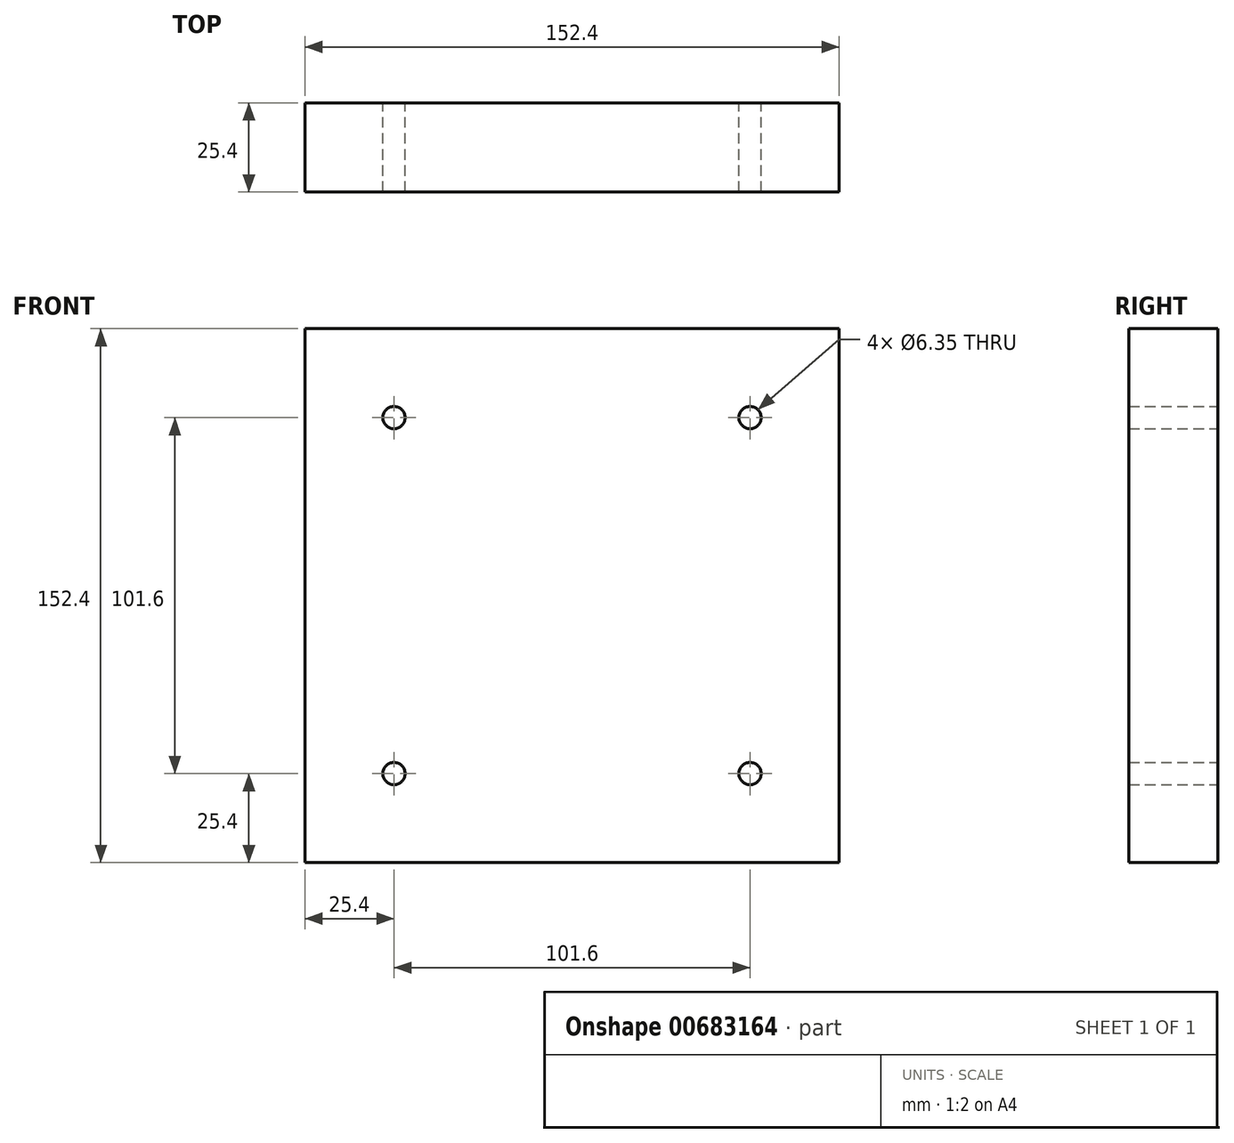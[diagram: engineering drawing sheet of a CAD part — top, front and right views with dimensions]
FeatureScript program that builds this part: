
annotation { "Feature Type Name" : "Feature", "Feature Type Description" : "" }
export const myFeature = defineFeature(function(context is Context, id is Id, definition is map)
    precondition{}
    {
        {
            var Q0;
            Q0=qCreatedBy(makeId("Front.planeOp"),FACE);
            var sketch = newSketch(context, id + "F0", { "sketchPlane" : qUnion([Q0])});
            skLineSegment(sketch, "E0.bottom", {"start": v(76.2, -76.2) * mm, "end": v(-76.2, -76.2) * mm});
            skLineSegment(sketch, "E0.top", {"start": v(76.2, 76.2) * mm, "end": v(-76.2, 76.2) * mm});
            skLineSegment(sketch, "E0.left", {"start": v(76.2, -76.2) * mm, "end": v(76.2, 76.2) * mm});
            skLineSegment(sketch, "E0.right", {"start": v(-76.2, -76.2) * mm, "end": v(-76.2, 76.2) * mm});
            skPoint(sketch, "E0.middle", {"position": v(0, 0) * mm});
            skLineSegment(sketch, "E1.bottom", {"start": v(50.8, 50.8) * mm, "end": v(-50.8, 50.8) * mm, "construction": true});
            skLineSegment(sketch, "E1.top", {"start": v(50.8, -50.8) * mm, "end": v(-50.8, -50.8) * mm, "construction": true});
            skLineSegment(sketch, "E1.left", {"start": v(50.8, 50.8) * mm, "end": v(50.8, -50.8) * mm, "construction": true});
            skLineSegment(sketch, "E1.right", {"start": v(-50.8, 50.8) * mm, "end": v(-50.8, -50.8) * mm, "construction": true});
            skCircle(sketch, "E2", {"center": v(-50.8, 50.8) * mm, "radius": 3.18 * mm});
            skCircle(sketch, "E3", {"center": v(50.8, 50.8) * mm, "radius": 3.18 * mm});
            skCircle(sketch, "E4", {"center": v(50.8, -50.8) * mm, "radius": 3.18 * mm});
            skCircle(sketch, "E5", {"center": v(-50.8, -50.8) * mm, "radius": 3.18 * mm});
            skSolve(sketch);
        }
        {
            var Q0;
            Q0=makeQuery(id+"F0.imprint","IMPRINT",FACE,{"disambiguationData":[TD([[makeQuery(id+"F0.imprint","IMPRINT",EDGE,{"derivedFrom":sQuery(id+"F0.wireOp",EDGE,"E0.bottom")}),-1.0]])]});
            extrude(context, id + "F1", {"entities" : qUnion([Q0]), "depth" : 25.4 * mm, "offsetDistance" : 25.4 * mm});
        }
    });
